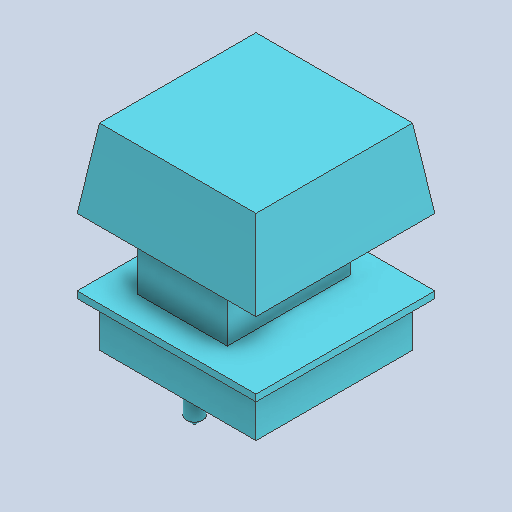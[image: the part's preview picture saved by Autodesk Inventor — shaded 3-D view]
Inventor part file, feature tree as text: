
AUTODESK INVENTOR PART (.ipt)
format: ipt  version: 2025.2 (Build 292293000, 293)  size: 164,352 bytes
history: native  units: mm
features: extrude x5, sketch x5, chamfer x2
ambient origin geometry x8: Origin, YZ Plane, XZ Plane, XY Plane, X Axis, Y Axis, Z Axis, Center Point
bodies: Solid1 (feature_tree)
feature tree (12):
  extrude  "Extrusion1"  Depth=14.0mm
  extrude  "Extrusion2"  Depth=16.0mm
  extrude  "Extrusion3"  Depth=0.6mm TaperAngle=0.0deg
  extrude  "Extrusion4"  Depth=11.0mm
  chamfer  "Chamfer1"  Distance=6.0mm
  extrude  "Extrusion5"  Depth=16.0mm
  chamfer  "Chamfer2"  Distance=7.0mm
  sketch  "Sketch1"  dims[d0=14.0mm d1=14.0mm]
  sketch  "Sketch2"  dims[d2=4.0mm d3=0.0mm d4=16.0mm]
  sketch  "Sketch3"  dims[d5=16.0mm d6=0.6mm d7=0.0mm]
  sketch  "Sketch4"  dims[d8=8.0mm d9=11.0mm d10=6.0mm d11=0.0mm]
  sketch  "Sketch5"  dims[d12=16.0mm d13=16.0mm d14=7.0mm d15=0.0mm d16=1.0mm d17=7.0mm d18=13.962634mm d19=4.0mm d22=1.5mm d23=5.5mm d24=3.0mm d25=0.0mm d26=0.7mm d27=6.0mm d28=13.962634mm]
